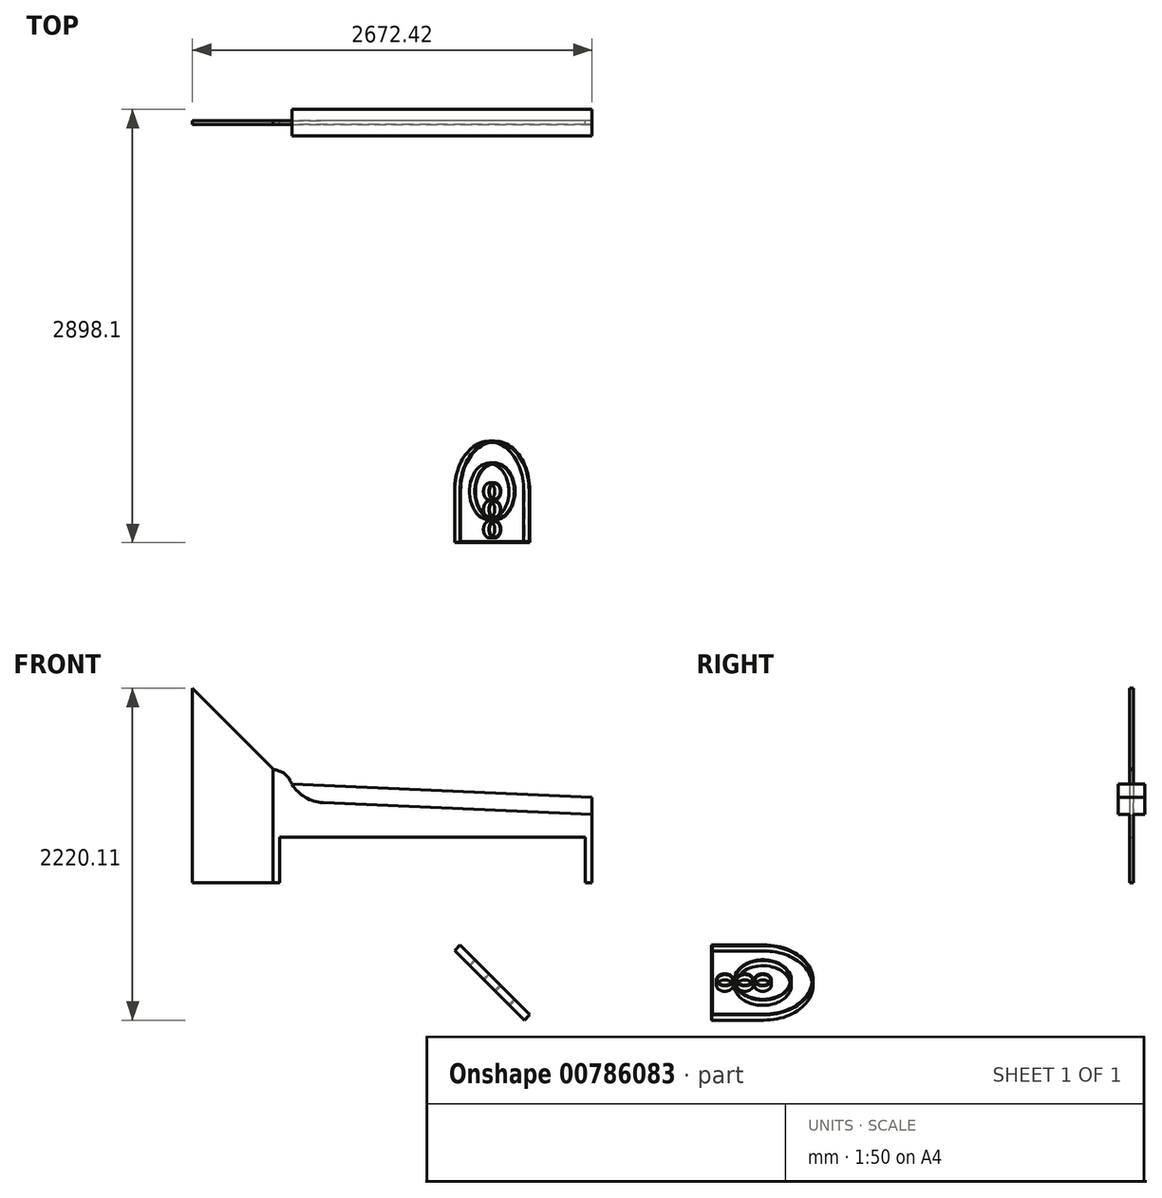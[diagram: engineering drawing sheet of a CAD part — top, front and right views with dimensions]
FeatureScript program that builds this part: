
annotation { "Feature Type Name" : "Feature", "Feature Type Description" : "" }
export const myFeature = defineFeature(function(context is Context, id is Id, definition is map)
    precondition{}
    {
        {
            assignVariable(context, id + "F0", {"name" : "width", "anyValue" : 26});
        }
        {
            var Q0;
            Q0=qCreatedBy(makeId("Front.planeOp"),FACE);
            var sketch = newSketch(context, id + "F1", { "sketchPlane" : qUnion([Q0])});
            skLineSegment(sketch, "E0", {"start": v(0, 0) * mm, "end": v(0, 457.2) * mm});
            skLineSegment(sketch, "E1", {"start": v(0, 457.2) * mm, "end": v(-1799.17, 535.75) * mm});
            skLineSegment(sketch, "E2", {"start": v(0, 0) * mm, "end": v(-44.45, 0) * mm});
            skLineSegment(sketch, "E3", {"start": v(-44.45, 0) * mm, "end": v(-44.45, 304.8) * mm});
            skLineSegment(sketch, "E4", {"start": v(-44.45, 304.8) * mm, "end": v(-2089.15, 304.8) * mm});
            skLineSegment(sketch, "E5", {"start": v(-2089.15, 304.8) * mm, "end": v(-2089.15, 0) * mm});
            skLineSegment(sketch, "E6", {"start": v(-2089.15, 0) * mm, "end": v(-2133.6, 0) * mm});
            skArc(sketch, "E7", {"start": v(-1799.17, 535.75) * mm, "mid": v(-1929.33, 578.36) * mm, "end": v(-2018.5, 682.3) * mm});
            skArc(sketch, "E8", {"start": v(-2018.5, 682.3) * mm, "mid": v(-2065.36, 735.74) * mm, "end": v(-2133.6, 755.63) * mm});
            skLineSegment(sketch, "E9", {"start": v(-2018.5, 682.3) * mm, "end": v(-2147.31, 958.55) * mm, "construction": true});
            skLineSegment(sketch, "E10", {"start": v(-2133.6, 755.63) * mm, "end": v(-2133.6, 0) * mm});
            skSolve(sketch);
        }
        {
            var Q0;
            Q0=makeQuery(id+"F1.imprint","IMPRINT",FACE,{"disambiguationData":[TD([[makeQuery(id+"F1.imprint","IMPRINT",EDGE,{"derivedFrom":sQuery(id+"F1.wireOp",EDGE,"E0")}),1.0]])]});
            extrude(context, id + "F2", {"entities" : qUnion([Q0]), "endBound" : BoundingType.SYMMETRIC, "depth" : (getVariable(context, 'width')) * mm, "offsetDistance" : 25.4 * mm});
        }
        {
            var Q0;
            Q0=qCreatedBy(makeId("Front.planeOp"),FACE);
            var sketch = newSketch(context, id + "F3", { "sketchPlane" : qUnion([Q0])});
            skLineSegment(sketch, "E11", {"start": v(-2133.6, 0) * mm, "end": v(-2133.6, 762) * mm});
            skLineSegment(sketch, "E12", {"start": v(-2133.6, 762) * mm, "end": v(-2672.42, 1300.82) * mm});
            skLineSegment(sketch, "E13", {"start": v(-2672.42, 1300.82) * mm, "end": v(-2672.42, 0) * mm});
            skLineSegment(sketch, "E14", {"start": v(-2672.42, 0) * mm, "end": v(-2133.6, 0) * mm});
            skSolve(sketch);
        }
        {
            var Q0;
            Q0 = qSketchRegion(id + "F3", true);
            extrude(context, id + "F4", {"entities" : qUnion([Q0]), "endBound" : BoundingType.SYMMETRIC, "depth" : (getVariable(context, 'width')) * mm, "offsetDistance" : 25.4 * mm});
        }
        {
            var Q0;
            Q0=makeQuery(id+"F4.opExtrude","SWEPT_FACE",FACE,{"disambiguationData":[OSD([sQuery(id+"F3.wireOp",EDGE,"E12")])]});
            var sketch = newSketch(context, id + "F5", { "sketchPlane" : qUnion([Q0])});
            skCircle(sketch, "E15", {"center": v(-2587.25, 0) * mm, "radius": 50.8 * mm});
            skCircle(sketch, "E16", {"center": v(-2466.6, 0) * mm, "radius": 50.8 * mm});
            skCircle(sketch, "E17", {"center": v(-2345.95, 0) * mm, "radius": 50.8 * mm});
            skCircle(sketch, "E18", {"center": v(-2199.9, 0) * mm, "radius": 50.8 * mm});
            skArc(sketch, "E19", {"start": v(-2460.25, -330.2) * mm, "mid": v(-2130.05, 0) * mm, "end": v(-2460.25, 330.2) * mm});
            skPoint(sketch, "E20", {"position": v(-2130.05, 0) * mm});
            skArc(sketch, "E21.0", {"start": v(-2460.25, -323.85) * mm, "mid": v(-2136.4, 0) * mm, "end": v(-2460.25, 323.85) * mm});
            skPoint(sketch, "E22", {"position": v(-2136.4, 0) * mm});
            skLineSegment(sketch, "E23", {"start": v(-2460.25, -330.2) * mm, "end": v(-2809.5, -330.2) * mm});
            skLineSegment(sketch, "E24", {"start": v(-2809.5, -330.2) * mm, "end": v(-2809.5, 330.2) * mm});
            skLineSegment(sketch, "E25", {"start": v(-2809.5, 330.2) * mm, "end": v(-2460.25, 330.2) * mm});
            skLineSegment(sketch, "E26", {"start": v(-2460.25, 323.85) * mm, "end": v(-2803.15, 323.85) * mm});
            skLineSegment(sketch, "E27", {"start": v(-2803.15, 323.85) * mm, "end": v(-2803.15, -323.85) * mm});
            skLineSegment(sketch, "E28", {"start": v(-2803.15, -323.85) * mm, "end": v(-2460.25, -323.85) * mm});
            skCircle(sketch, "E29.0", {"center": v(-2466.6, 0) * mm, "radius": 57.15 * mm});
            skCircle(sketch, "E30.0", {"center": v(-2587.25, 0) * mm, "radius": 57.15 * mm});
            skCircle(sketch, "E31", {"center": v(-2466.6, 0) * mm, "radius": 184.15 * mm});
            skPoint(sketch, "E32", {"position": v(-2650.75, 0) * mm});
            skPoint(sketch, "E33", {"position": v(-2282.45, 0) * mm});
            skPoint(sketch, "E34", {"position": v(-2295.15, 0) * mm});
            skPoint(sketch, "E35", {"position": v(-2644.4, 0) * mm});
            skCircle(sketch, "E36.0", {"center": v(-2466.6, 0) * mm, "radius": 190.5 * mm});
            skCircle(sketch, "E37", {"center": v(-2720.6, 0) * mm, "radius": 50.8 * mm});
            skCircle(sketch, "E38.0", {"center": v(-2720.6, 0) * mm, "radius": 57.15 * mm});
            skSolve(sketch);
        }
        {
            var Q0;
            Q0=makeQuery(id+"F5.imprint","IMPRINT",FACE,{"disambiguationData":[TD([[makeQuery(id+"F5.imprint","IMPRINT",EDGE,{"derivedFrom":sQuery(id+"F5.wireOp",EDGE,"E19")}),1.0]])]});
            var Q1;
            Q1=makeQuery(id+"F5.imprint","IMPRINT",FACE,{"disambiguationData":[TD([[makeQuery(id+"F5.imprint","IMPRINT",EDGE,{"derivedFrom":sQuery(id+"F5.wireOp",EDGE,"E31")}),-1.0]])]});
            var Q2;
            Q2=makeQuery(id+"F5.imprint","IMPRINT",FACE,{"disambiguationData":[TD([[makeQuery(id+"F5.imprint","IMPRINT",EDGE,{"derivedFrom":sQuery(id+"F5.wireOp",EDGE,"E16")}),-1.0]])]});
            var Q3;
            Q3=makeQuery(id+"F5.imprint","IMPRINT",FACE,{"disambiguationData":[TD([[makeQuery(id+"F5.imprint","IMPRINT",EDGE,{"derivedFrom":sQuery(id+"F5.wireOp",EDGE,"E15")}),-1.0]])]});
            var Q4;
            Q4=makeQuery(id+"F5.imprint","IMPRINT",FACE,{"disambiguationData":[TD([[makeQuery(id+"F5.imprint","IMPRINT",EDGE,{"derivedFrom":sQuery(id+"F5.wireOp",EDGE,"E37")}),-1.0]])]});
            extrude(context, id + "F6", {"entities" : qUnion([Q0, Q1, Q2, Q3, Q4]), "operationType" : NewBodyOperationType.ADD, "depth" : 50.8 * mm, "offsetDistance" : 25.4 * mm});
        }
        {
            var Q0;
            Q0=makeQuery(id+"F5.imprint","IMPRINT",FACE,{"disambiguationData":[TD([[makeQuery(id+"F5.imprint","IMPRINT",EDGE,{"derivedFrom":sQuery(id+"F5.wireOp",EDGE,"E18")}),1.0]])]});
            var Q1;
            Q1=makeQuery(id+"F5.imprint","IMPRINT",FACE,{"disambiguationData":[TD([[makeQuery(id+"F5.imprint","IMPRINT",EDGE,{"derivedFrom":sQuery(id+"F5.wireOp",EDGE,"E17")}),1.0]])]});
            extrude(context, id + "F7", {"entities" : qUnion([Q0, Q1]), "operationType" : NewBodyOperationType.REMOVE, "oppositeDirection" : true, "depth" : 25.4 * mm, "offsetDistance" : 25.4 * mm});
        }
        {
            var Q0;
            Q0=makeQuery(id+"F2.opExtrude","CAP_FACE",FACE,{"disambiguationData":[OSD([sQuery(id+"F1.wireOp",EDGE,"E0"),sQuery(id+"F1.wireOp",EDGE,"E1"),sQuery(id+"F1.wireOp",EDGE,"E2"),sQuery(id+"F1.wireOp",EDGE,"E3"),sQuery(id+"F1.wireOp",EDGE,"E4"),sQuery(id+"F1.wireOp",EDGE,"E5"),sQuery(id+"F1.wireOp",EDGE,"E6"),sQuery(id+"F1.wireOp",EDGE,"E7"),sQuery(id+"F1.wireOp",EDGE,"E8"),sQuery(id+"F1.wireOp",EDGE,"E10")])],"isStart":false});
            var sketch = newSketch(context, id + "F8", { "sketchPlane" : qUnion([Q0])});
            skLineSegment(sketch, "E39.0", {"start": v(0, 457.2) * mm, "end": v(-1799.17, 535.75) * mm});
            skLineSegment(sketch, "E40", {"start": v(0, 457.2) * mm, "end": v(0, 571.5) * mm});
            skLineSegment(sketch, "E41", {"start": v(0, 571.5) * mm, "end": v(-2006.17, 659.1) * mm});
            skArc(sketch, "E42.0", {"start": v(-1799.17, 535.75) * mm, "mid": v(-1929.33, 578.36) * mm, "end": v(-2018.5, 682.3) * mm});
            skSolve(sketch);
        }
        {
            var Q0;
            {var subQ0=sQuery(id+"F8.wireOp",EDGE,"E39.0");Q0=makeQuery(id+"F8.imprint","IMPRINT",FACE,{"disambiguationData":[TD([[makeQuery(id+"F8.imprint","IMPRINT",EDGE,{"derivedFrom":subQ0}),-1.0]])]});}
            extrude(context, id + "F9", {"entities" : qUnion([Q0]), "operationType" : NewBodyOperationType.ADD, "oppositeDirection" : true, "depth" : 101.6 * mm, "offsetDistance" : 25.4 * mm});
        }
        {
            var Q0;
            Q0=makeQuery(id+"F2.opExtrude","CAP_FACE",FACE,{"disambiguationData":[OSD([sQuery(id+"F1.wireOp",EDGE,"E0"),sQuery(id+"F1.wireOp",EDGE,"E1"),sQuery(id+"F1.wireOp",EDGE,"E2"),sQuery(id+"F1.wireOp",EDGE,"E3"),sQuery(id+"F1.wireOp",EDGE,"E4"),sQuery(id+"F1.wireOp",EDGE,"E5"),sQuery(id+"F1.wireOp",EDGE,"E6"),sQuery(id+"F1.wireOp",EDGE,"E7"),sQuery(id+"F1.wireOp",EDGE,"E8"),sQuery(id+"F1.wireOp",EDGE,"E10")])],"isStart":true});
            var sketch = newSketch(context, id + "F10", { "sketchPlane" : qUnion([Q0])});
            skLineSegment(sketch, "E43.0.0", {"start": v(0, 571.5) * mm, "end": v(0, 457.2) * mm});
            skLineSegment(sketch, "E43.0.1", {"start": v(0, 457.2) * mm, "end": v(1799.17, 535.75) * mm});
            skArc(sketch, "E43.0.2", {"start": v(1799.17, 535.75) * mm, "mid": v(1918.21, 571.34) * mm, "end": v(2006.17, 659.1) * mm});
            skLineSegment(sketch, "E43.0.3", {"start": v(2006.17, 659.1) * mm, "end": v(0, 571.5) * mm});
            skSolve(sketch);
        }
        {
            var Q0;
            Q0=makeQuery(id+"F10.imprint","IMPRINT",FACE,{"disambiguationData":[TD([[makeQuery(id+"F10.imprint","IMPRINT",EDGE,{"derivedFrom":sQuery(id+"F10.wireOp",EDGE,"E43.0.0")}),1.0]])]});
            extrude(context, id + "F11", {"entities" : qUnion([Q0]), "operationType" : NewBodyOperationType.ADD, "oppositeDirection" : true, "depth" : 101.6 * mm, "offsetDistance" : 25.4 * mm});
        }
    });
